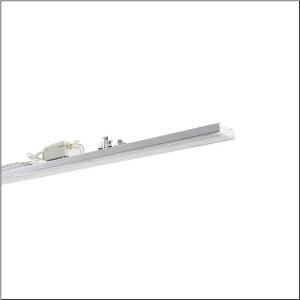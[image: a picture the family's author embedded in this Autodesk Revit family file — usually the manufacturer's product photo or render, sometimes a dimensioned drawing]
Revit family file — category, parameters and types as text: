
# Revit family: licross_r__11_recessed_mo_51tl19mn495g_cade
name_source: partatom
category: Lighting Fixtures
units: mm (PartAtom-declared; Revit-internal decimal feet)

## family parameters
Cut with Voids When Loaded = No
Host = Face
Light Source = No
Part Type = Normal
Room Calculation Point = No
Round Connector Dimension = Use Diameter
Shared = No

## types (1)
- --- (1 x LED, 9850 lm, 55.2 W, 4000K)
    Apparent Load = 55 VA
    CIE Flux Codes = 55 90 98 100 100
    Color Rendering = 80
    Color Temperature = 4000K
    Default Elevation = 1800 mm
    Description = Licross® 11 Recessed MO, luminaire insert, of sheet steel, coil coated, white, length: 1.500mm, width: 66mm, height: 67mm, LED rated luminous flux: 9.860lm, light colour: 840, control gear: ON/OFF Multilumen, with plug, 3-pole, with phase selection, mains connection: 220..240V, AC, 50/60Hz, rated input power: 55W, halogen-free wiring, primary light control with lens, of plastic, primary optical cover: cover, of PMMA, light emission: direct distribution, primary light characteristic: double asymmetric, protection rating (complete): IP40, insulation class (complete): insulation class I (protective earthing), certification: CE, ENEC, VDE, UKCA, protection symbol: D if used in an environment without relevant dust loads with corresponding accessories, impact resistance: IK06, permissible ambient temperature for indoor applications: -35..+40°C, corresponds to IFS (International Featured Standards) requirements for safety and quality in the food industry, reducing of maximum allowable ambient temperature of 5°C with ceiling mounting, packaging unit: 1 piece
    Height = 58 mm
    Lamp = 1 x LED
    Lamp Light Flux = 9850 lm
    Lamp Power = 55.2 W
    Lamp count = 1
    Length = 1500 mm
    Luminous efficacy = 178 lm/W
    Manufacturer = Siteco
    ModVariant = No
    Model = 51TL19MN495G
    Mounting Place = Ceiling
    Mounting Type = Pendant
    Number of Poles = 1
    OnlyDefault = Yes
    Power Factor = 1
    Product Name = Licross® 11 Recessed MO
    Product group = luminaire insert
    ProductGroupID = 901
    Protection Class = Protection class I
    Protection Degree = IP 40
    RLX_Detail_Level = 1
    RLX_Emergency_Light_Flux = 0 lm
    RLX_Emergency_Type = 0
    RLX_Emergency_Type_DB = No
    RlxData = <blob elided: 22185 chars, md5=1c2dc996>
    Socket = socket
    Standby Power = 0 W
    System Light Flux = 9850 lm
    System Power = 55 W
    Type Comments = factory setting: luminous flux: 100 % | (A | C | E) | 126 mA
    Type Image = l_1296930.jpg
    URL = http://relux.com
    VarID = @adj_055023
    Voltage = 0 V
    Weight = 0.00 kg
    Width = 66 mm

## geometry (parser evidence)
native form markers: Blend x4, Sweep x9
no freeform markers — native parametric forms only
